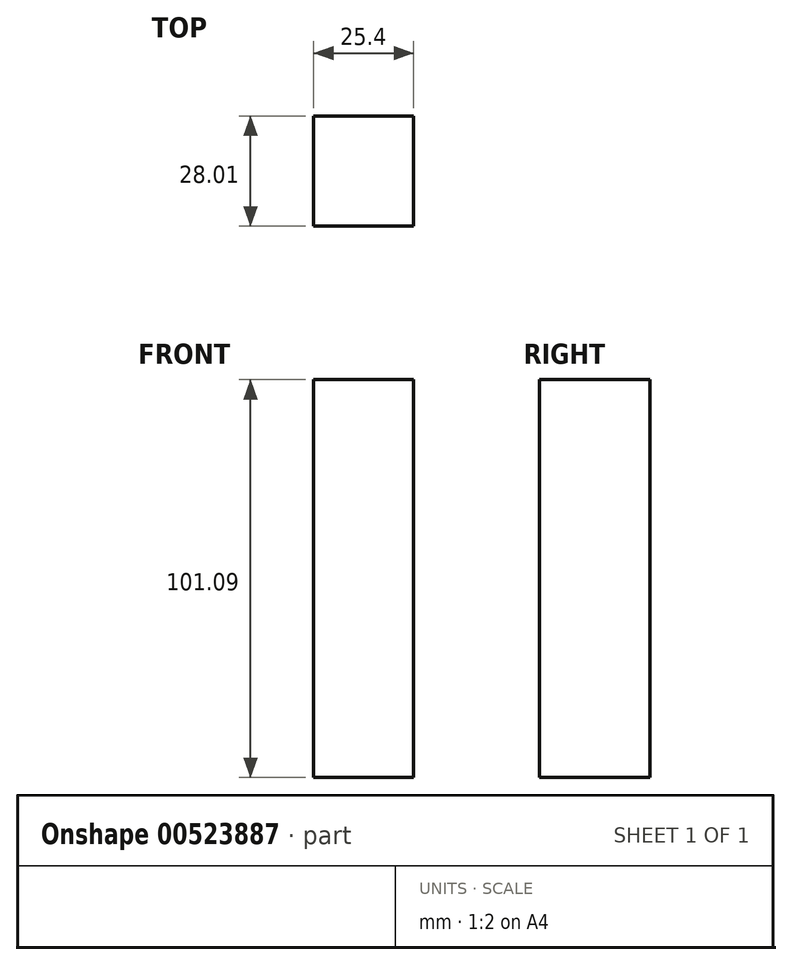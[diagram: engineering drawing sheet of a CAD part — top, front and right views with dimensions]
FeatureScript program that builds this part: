
annotation { "Feature Type Name" : "Feature", "Feature Type Description" : "" }
export const myFeature = defineFeature(function(context is Context, id is Id, definition is map)
    precondition{}
    {
        {
            var Q0;
            Q0=qCreatedBy(makeId("Right.planeOp"),FACE);
            var sketch = newSketch(context, id + "F0", { "sketchPlane" : qUnion([Q0])});
            skLineSegment(sketch, "E0.bottom", {"start": v(0, 0) * mm, "end": v(28, 0) * mm});
            skLineSegment(sketch, "E0.top", {"start": v(0, 101.1) * mm, "end": v(28, 101.1) * mm});
            skLineSegment(sketch, "E0.left", {"start": v(0, 0) * mm, "end": v(0, 101.1) * mm});
            skLineSegment(sketch, "E0.right", {"start": v(28, 0) * mm, "end": v(28, 101.1) * mm});
            skSolve(sketch);
        }
        {
            var Q0;
            Q0=makeQuery(id+"F0.imprint","IMPRINT",FACE,{"disambiguationData":[TD([[makeQuery(id+"F0.imprint","IMPRINT",EDGE,{"derivedFrom":sQuery(id+"F0.wireOp",EDGE,"E0.bottom")}),1.0]])]});
            var sketch = newSketch(context, id + "F1", { "sketchPlane" : qUnion([Q0])});
            skArc(sketch, "E1", {"start": v(-47.09, -45.77) * mm, "mid": v(57.27, -1.77) * mm, "end": v(-55.97, 0) * mm});
            skSolve(sketch);
        }
        {
            var Q0;
            Q0 = qSketchRegion(id + "F1", true);
            var Q1;
            Q1=makeQuery(id+"F0.imprint","IMPRINT",FACE,{"disambiguationData":[TD([[makeQuery(id+"F0.imprint","IMPRINT",EDGE,{"derivedFrom":sQuery(id+"F0.wireOp",EDGE,"E0.bottom")}),1.0]])]});
            extrude(context, id + "F2", {"entities" : qUnion([Q0, Q1]), "depth" : 25.4 * mm, "offsetDistance" : 25.4 * mm});
        }
    });
